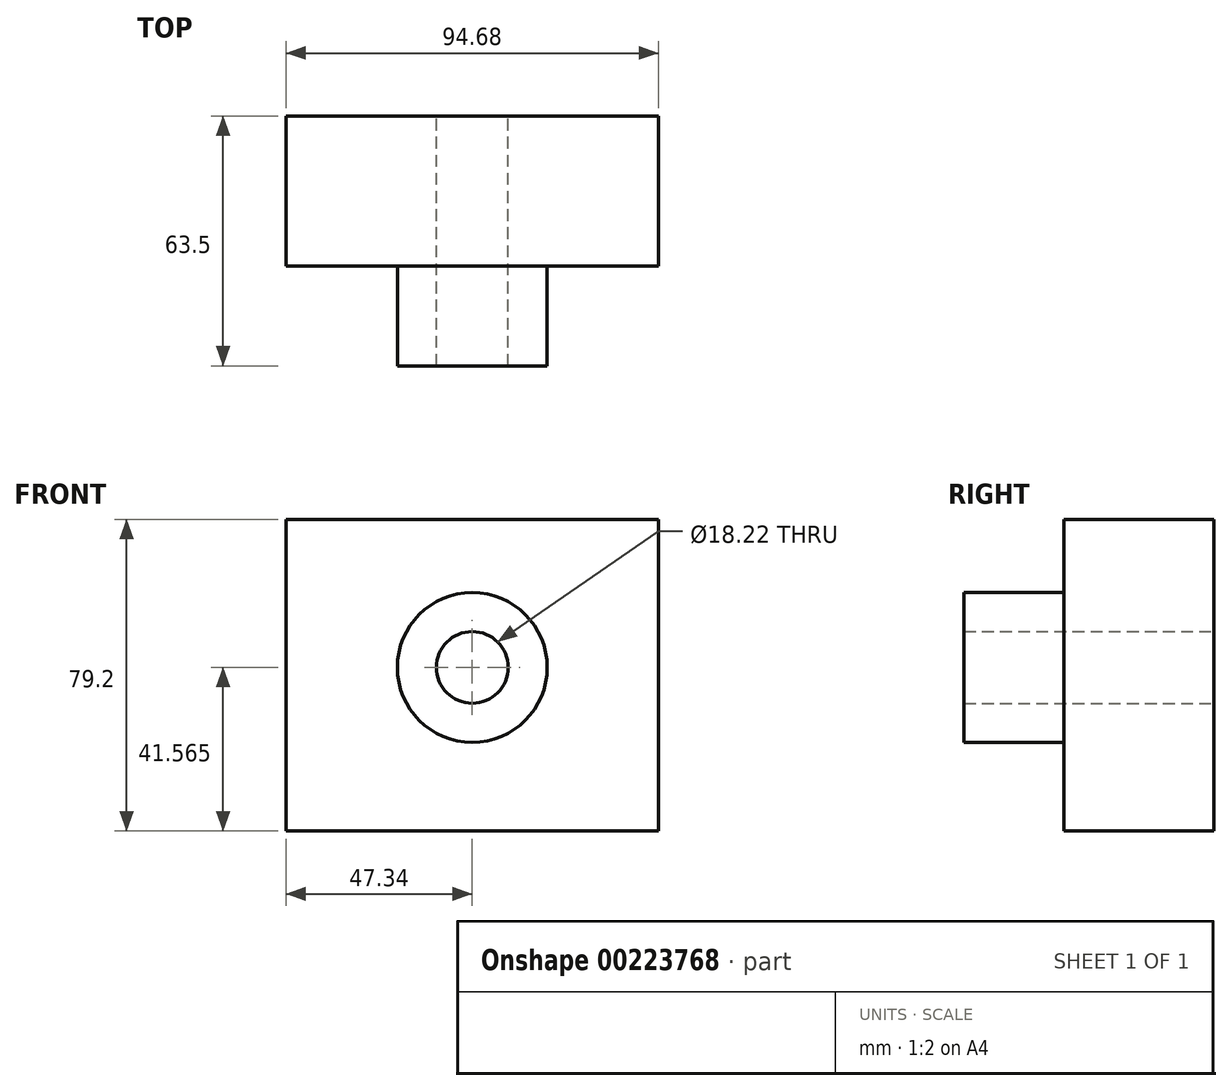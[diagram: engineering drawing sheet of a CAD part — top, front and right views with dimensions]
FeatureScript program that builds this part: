
annotation { "Feature Type Name" : "Feature", "Feature Type Description" : "" }
export const myFeature = defineFeature(function(context is Context, id is Id, definition is map)
    precondition{}
    {
        {
            var Q0;
            Q0=qCreatedBy(makeId("Front.planeOp"),FACE);
            var sketch = newSketch(context, id + "F0", { "sketchPlane" : qUnion([Q0])});
            skLineSegment(sketch, "E0.bottom", {"start": v(-47.34, 27.36) * mm, "end": v(47.34, 27.36) * mm});
            skLineSegment(sketch, "E0.top", {"start": v(-47.34, -51.84) * mm, "end": v(47.34, -51.84) * mm});
            skLineSegment(sketch, "E0.left", {"start": v(-47.34, 27.36) * mm, "end": v(-47.34, -51.84) * mm});
            skLineSegment(sketch, "E0.right", {"start": v(47.34, 27.36) * mm, "end": v(47.34, -51.84) * mm});
            skSolve(sketch);
        }
        {
            var Q0;
            Q0=makeQuery(id+"F0.imprint","IMPRINT",FACE,{"disambiguationData":[TD([[makeQuery(id+"F0.imprint","IMPRINT",EDGE,{"derivedFrom":sQuery(id+"F0.wireOp",EDGE,"E0.bottom")}),-1.0]])]});
            extrude(context, id + "F1", {"entities" : qUnion([Q0]), "depth" : 12.7 * mm});
        }
        {
            var Q0;
            Q0=makeQuery(id+"F1.opExtrude","CAP_FACE",FACE,{"disambiguationData":[OSD([sQuery(id+"F0.wireOp",EDGE,"E0.bottom"),sQuery(id+"F0.wireOp",EDGE,"E0.top"),sQuery(id+"F0.wireOp",EDGE,"E0.left"),sQuery(id+"F0.wireOp",EDGE,"E0.right")])],"isStart":false});
            extrude(context, id + "F2", {"entities" : qUnion([Q0]), "operationType" : NewBodyOperationType.ADD, "depth" : 25.4 * mm});
        }
        {
            var Q0;
            Q0=makeQuery(id+"F2.opExtrude","CAP_FACE",FACE,{"disambiguationData":[OSD([sQuery(id+"F0.wireOp",EDGE,"E0.bottom"),sQuery(id+"F0.wireOp",EDGE,"E0.top"),sQuery(id+"F0.wireOp",EDGE,"E0.left"),sQuery(id+"F0.wireOp",EDGE,"E0.right")])],"isStart":false});
            var sketch = newSketch(context, id + "F3", { "sketchPlane" : qUnion([Q0])});
            skCircle(sketch, "E1", {"center": v(0, -10.28) * mm, "radius": 19.04 * mm});
            skCircle(sketch, "E2", {"center": v(0, -10.28) * mm, "radius": 9.1 * mm});
            skSolve(sketch);
        }
        {
            var Q0;
            Q0=makeQuery(id+"F3.imprint","IMPRINT",FACE,{"disambiguationData":[TD([[makeQuery(id+"F3.imprint","IMPRINT",EDGE,{"derivedFrom":sQuery(id+"F3.wireOp",EDGE,"E1")}),1.0]])]});
            extrude(context, id + "F4", {"entities" : qUnion([Q0]), "operationType" : NewBodyOperationType.ADD, "depth" : 25.4 * mm});
        }
        {
            var Q0;
            Q0=makeQuery(id+"F4.boolean.opBoolean","SPLIT",FACE,{"disambiguationData":[TD([makeQuery(id+"F4.opExtrude","SWEPT_FACE",FACE,{"disambiguationData":[OSD([sQuery(id+"F3.wireOp",EDGE,"E2")])]})])],"derivedFrom":makeQuery(id+"F2.opExtrude","CAP_FACE",FACE,{"disambiguationData":[OSD([sQuery(id+"F0.wireOp",EDGE,"E0.bottom"),sQuery(id+"F0.wireOp",EDGE,"E0.top"),sQuery(id+"F0.wireOp",EDGE,"E0.left"),sQuery(id+"F0.wireOp",EDGE,"E0.right")])],"isStart":false})});
            extrude(context, id + "F5", {"entities" : qUnion([Q0]), "operationType" : NewBodyOperationType.REMOVE, "endBound" : BoundingType.THROUGH_ALL, "oppositeDirection" : true, "depth" : 25.4 * mm});
        }
    });
